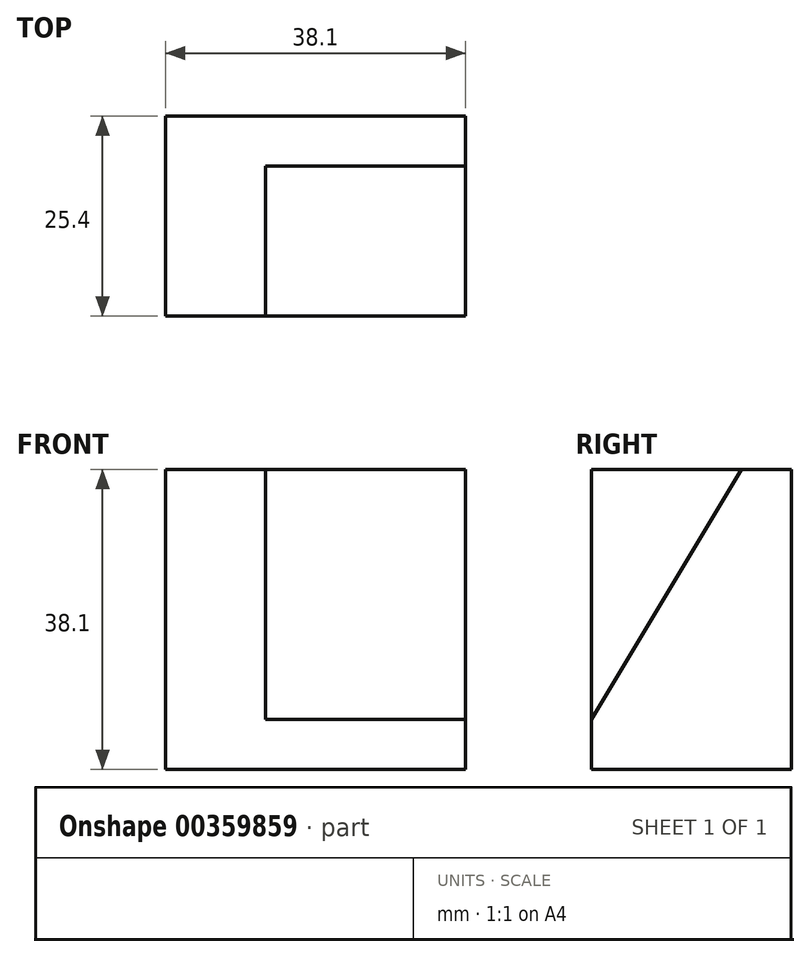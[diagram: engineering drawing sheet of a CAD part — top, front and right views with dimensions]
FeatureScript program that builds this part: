
annotation { "Feature Type Name" : "Feature", "Feature Type Description" : "" }
export const myFeature = defineFeature(function(context is Context, id is Id, definition is map)
    precondition{}
    {
        {
            var Q0;
            Q0=qCreatedBy(makeId("Front.planeOp"),FACE);
            var sketch = newSketch(context, id + "F0", { "sketchPlane" : qUnion([Q0])});
            skLineSegment(sketch, "E0", {"start": v(0, 0) * mm, "end": v(0, 38.1) * mm});
            skLineSegment(sketch, "E1", {"start": v(0, 38.1) * mm, "end": v(38.1, 38.1) * mm});
            skLineSegment(sketch, "E2", {"start": v(38.1, 38.1) * mm, "end": v(38.1, 0) * mm});
            skLineSegment(sketch, "E3", {"start": v(38.1, 0) * mm, "end": v(0, 0) * mm});
            skSolve(sketch);
        }
        {
            var Q0;
            Q0 = qSketchRegion(id + "F0", true);
            extrude(context, id + "F1", {"entities" : qUnion([Q0]), "depth" : 25.4 * mm});
        }
        {
            var Q0;
            Q0=makeQuery(id+"F1.opExtrude","SWEPT_FACE",FACE,{"disambiguationData":[OSD([sQuery(id+"F0.wireOp",EDGE,"E2")])]});
            var sketch = newSketch(context, id + "F2", { "sketchPlane" : qUnion([Q0])});
            skLineSegment(sketch, "E4", {"start": v(-6.35, 38.1) * mm, "end": v(-25.4, 6.35) * mm});
            skSolve(sketch);
        }
        {
            var Q0;
            {var subQ0=sQuery(id+"F2.wireOp",EDGE,"E4");Q0=makeQuery(id+"F2.imprint","IMPRINT",FACE,{"disambiguationData":[TD([[makeQuery(id+"F2.imprint","IMPRINT",EDGE,{"derivedFrom":subQ0}),-1.0]])]});}
            extrude(context, id + "F3", {"entities" : qUnion([Q0]), "operationType" : NewBodyOperationType.REMOVE, "oppositeDirection" : true, "depth" : 25.4 * mm});
        }
    });
